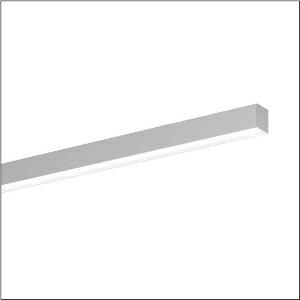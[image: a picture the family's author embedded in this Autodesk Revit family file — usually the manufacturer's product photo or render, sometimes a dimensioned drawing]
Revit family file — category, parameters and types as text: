
# Revit family: silica_r__21_51mx20tct5s_f80a
name_source: partatom
category: Lighting Fixtures
units: mm (PartAtom-declared; Revit-internal decimal feet)

## family parameters
Cut with Voids When Loaded = No
Host = Face
Light Source = No
Part Type = Normal
Room Calculation Point = No
Round Connector Dimension = Use Diameter
Shared = No

## types (1)
- --- (1 x LED, 6000 lm, 51.3 W, 6500K)
    Apparent Load = 51 VA
    CIE Flux Codes = 48 79 96 100 100
    Color Rendering = 80
    Color Temperature = 6500K
    Default Elevation = 1800 mm
    Description = Silica® 21, office luminaire, primary optical cover: cover, of PMMA, opal, light emission: direct distribution, primary light characteristic: symmetric, installation type: surface-mounted, LED, rated luminous flux: 6.000lm, luminous efficacy: 112lm/W, light colour: 8tw, colour temperature: 2700..6500K, control gear: ECG DALI, with terminal, 3+2-pole, max. 2.5mm², mains connection: 220..240V, AC, 50/60Hz, rated input power: 53.8W, luminaire housing, of aluminium, metallic grey (RAL 9006), length: 3.004mm, width: 53mm, height: 53mm, protection rating (complete): IP20, insulation class (complete): insulation class I (protective earthing), certification: CE, permissible operating ambient temperature: 0..+35°C, standard: EN 50419, packaging unit: 1 piece
    Height = 0 mm  [stored 0 ft]
    Lamp = 1 x LED
    Lamp Light Flux = 6000 lm
    Lamp Power = 51.3 W
    Lamp count = 1
    Length = 3004 mm
    Luminous efficacy = 117 lm/W
    Manufacturer = Siteco
    ModVariant = No
    Model = 51MX20TCT5S
    Mounting Place = Ceiling
    Mounting Type = Recessed
    Number of Poles = 1
    OnlyDefault = Yes
    Power Factor = 1
    Product Name = Silica® 21
    Product group = office luminaire | ceiling recessed
    ProductGroupID = 401
    Protection Class = Protection class I
    Protection Degree = IP 20
    RLX_Detail_Level = 1
    RLX_Emergency_Light_Flux = 0 lm
    RLX_Emergency_Type = 0
    RLX_Emergency_Type_DB = No
    RlxData = <blob elided: 23137 chars, md5=c2c00953>
    Socket = socket
    Standby Power = 0 W
    System Light Flux = 6000 lm
    System Power = 51 W
    Type Comments = individual setting
    Type Image = l_1297768.jpg
    URL = http://relux.com
    VarID = @adj_070987
    Voltage = 0 V
    Weight = 0.00 kg
    Width = 53 mm

note: [stored X ft] marks values corroborated as IEEE doubles in the binary element streams (Revit-internal decimal feet)

## geometry (parser evidence)
native form markers: Blend x4, Sweep x13
no freeform markers — native parametric forms only
